# Revit family: Domotics-DomesticRanges-GEWISS-SYSTEM_COMMAND-BLANKING_MODULE_HOLED
name_source: partatom
category: Apparecchi elettrici
revit_build: Autodesk Revit 2016 (Build: 20161004_0715(x64)
units: mm (PartAtom-declared; Revit-internal decimal feet)

## family parameters
Condiviso = Sì
Host = Superficie
Mantenere orientamento annotazione = Sì
Punto di calcolo locali = Sì
Quota connettore circolare = Usa diametro
Taglio con vuoti quando caricato = Sì
Tipo di parte = Normale

## types (2) — shared parameters
Carico apparente = 0 VA
Catalogue = DOMOTICS
Catalogue Range = SYSTEM - Special plates
Description: = 1 gang with outlet for cable Ã˜ 4 and Ã˜ 8mm
Electrocod = 0100
IDF = f39112c6-2c56-4437-931d-8b6510c2e479
IDT = 1d4c7369-90d9-4ee2-b0c1-1d2cf6ad4b98
Immagine tipo = GW21058.jpg
N. poli = 1
No. SYSTEM modules = 1
Produttore = GEWISS S.p.A.
Prospetto di default = 1219 mm
SEO = Cable outlet
TIPO = System Copriforo Uscita Cavo_GENERICO : GW21058 Copriforo 1 modulo uscita cavo nero
Technical sheet = https://www.gewiss.com
URL = https://www.gewiss.com
Version file RFA = 19.4
Volt = 230 V

## per-type parameters (varying)
| type | Colour | Descrizione | EAN code | Modello |
| GW21058 - BLANKING MODULE 1 GANG CORD OUT.SY/BK | Black | BLANKING MODULE 1 GANG CORD OUT.SY/BK | 8011564128248 | GW21058 |
| GW20058 - BLANKING MODULE 1 GANG CORD OUT.SY/WT | White | BLANKING MODULE 1 GANG CORD OUT.SY/WT | 8011564001220 | GW20058 |

## geometry (parser evidence)
native form markers: Blend x4, Sweep x1
no freeform markers — native parametric forms only
